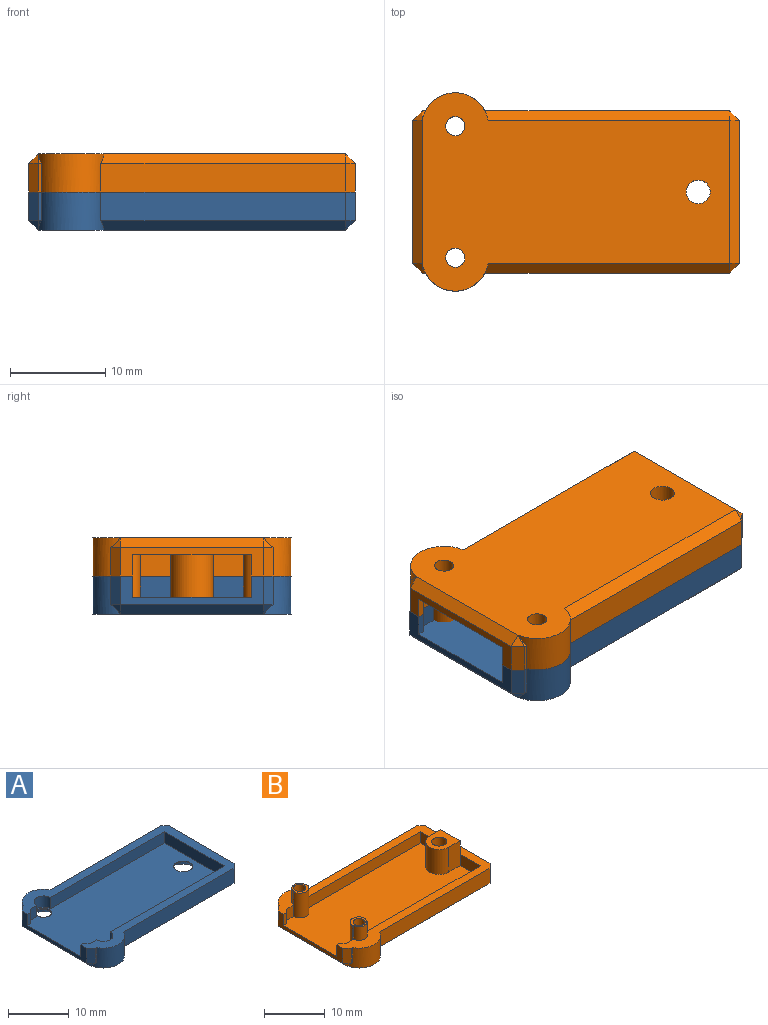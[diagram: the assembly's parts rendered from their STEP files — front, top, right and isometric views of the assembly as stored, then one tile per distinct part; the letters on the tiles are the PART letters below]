
ASSEMBLY  parts=2 mates=3
PART A: 42 faces, bbox 34.3x20.8x4 mm
  f0: plane 15x3mm, normal (-1,0,0), area 17.1mm2, adj f4,f13,f21,f22,f32,f35,f36
  f1: cylinder r=1.3mm len=2.6mm, axis (0,0,-1), area 2mm2, adj f22,f39
  f2: cylinder r=1.55mm len=3.1mm, axis (0,0,-1), area 1.5mm2, adj f22,f41
  f3: cylinder r=1.3mm len=2.6mm, axis (0,0,-1), area 2mm2, adj f22,f40
  f4: plane 34.25x20.8mm, normal (0,0,1), area 141.4mm2, adj f0,f5,f6,f7,f8,f9,f10,f11
  f5: plane 3x0.34mm, normal (0,-1,0), area 1mm2, adj f4,f6,f32,f33
  f6: cylinder r=3.5mm len=6.9mm, axis (0,0,-1), area 31.8mm2, adj f4,f5,f7,f12,f25,f33
  f7: plane 25.69x3mm, normal (0,-1,0), area 77.1mm2, adj f4,f6,f25,f26
  f8: plane 15x3mm, normal (1,0,0), area 45mm2, adj f4,f26,f28,f29
  f9: plane 25.69x3mm, normal (0,1,0), area 77.1mm2, adj f4,f10,f29,f31
  f10: cylinder r=3.5mm len=6.9mm, axis (0,0,-1), area 31.8mm2, adj f4,f9,f11,f12,f31,f38
  f11: plane 3x0.34mm, normal (0,1,0), area 1mm2, adj f4,f10,f35,f38
  f12: plane 32.25x20.8mm, normal (0,0,-1), area 433.4mm2, adj f6,f10,f25,f28,f31,f33,f36,f38
  f13: plane 2.25x0.7mm, normal (0,1,0), area 1.6mm2, adj f0,f4,f22,f23
  f14: plane 2.25x1.45mm, normal (0,1,0), area 3.3mm2, adj f4,f15,f22,f23
  f15: cylinder r=1.6mm len=3.2mm, axis (0,0,1), area 11.3mm2, adj f4,f14,f16,f22
  f16: plane 26.5x2.25mm, normal (0,1,0), area 59.6mm2, adj f4,f15,f17,f22
  f17: plane 13.8x2.25mm, normal (-1,0,0), area 31mm2, adj f4,f16,f18,f22
  f18: plane 26.5x2.25mm, normal (0,-1,0), area 59.6mm2, adj f4,f17,f19,f22
  f19: cylinder r=1.6mm len=3.2mm, axis (0,0,1), area 11.3mm2, adj f4,f18,f20,f22
  f20: plane 2.25x1.45mm, normal (0,-1,0), area 3.3mm2, adj f4,f19,f22,f24
  f21: plane 2.25x0.7mm, normal (0,-1,0), area 1.6mm2, adj f0,f4,f22,f24
  f22: plane 32.55x17mm, normal (0,0,1), area 437.6mm2, adj f0,f1,f2,f3,f13,f14,f15,f16
  f23: plane 2.25x0.7mm, normal (0.71,0.71,0), area 2.2mm2, adj f4,f13,f14,f22
  f24: plane 2.25x0.7mm, normal (0.71,-0.71,0), area 2.2mm2, adj f4,f20,f21,f22
  f25: plane 25.69x1mm, normal (0,-0.71,-0.71), area 36.1mm2, adj f6,f7,f12,f27
  f26: plane 3x1mm, normal (0.71,-0.71,0), area 4.2mm2, adj f4,f7,f8,f27
  f27: plane 1x1mm, normal (0.58,-0.58,-0.58), area 0.9mm2, adj f25,f26,f28
  f28: plane 15x1mm, normal (0.71,0,-0.71), area 21.2mm2, adj f8,f12,f27,f30
  f29: plane 3x1mm, normal (0.71,0.71,0), area 4.2mm2, adj f4,f8,f9,f30
  f30: plane 1x1mm, normal (0.58,0.58,-0.58), area 0.9mm2, adj f28,f29,f31
  f31: plane 25.69x1mm, normal (0,0.71,-0.71), area 36.1mm2, adj f9,f10,f12,f30
  f32: plane 3x1mm, normal (-0.71,-0.71,0), area 4.2mm2, adj f0,f4,f5,f34
  f33: plane 1x1mm, normal (0,-0.71,-0.71), area 0.2mm2, adj f5,f6,f12,f34
  f34: plane 1x1mm, normal (-0.58,-0.58,-0.58), area 0.9mm2, adj f32,f33,f36
  f35: plane 3x1mm, normal (-0.71,0.71,0), area 4.2mm2, adj f0,f4,f11,f37
  f36: plane 15x1mm, normal (-0.71,0,-0.71), area 21.2mm2, adj f0,f12,f34,f37
  f37: plane 1x1mm, normal (-0.58,0.58,-0.58), area 0.9mm2, adj f35,f36,f38
  f38: plane 1x1mm, normal (0,0.71,-0.71), area 0.2mm2, adj f10,f11,f12,f37
  f39: cone r=2.8mm half-angle=45deg, axis (0,0,-1), area 27.3mm2, adj f1,f12
  f40: cone r=1.3mm half-angle=45deg, axis (0,0,-1), area 27.3mm2, adj f3,f12
  f41: cone r=3.15mm half-angle=45deg, axis (0,0,-1), area 33.4mm2, adj f2,f12
PART B: 53 faces, bbox 34.3x20.8x6.8 mm
  f0: plane 26.6x2.25mm, normal (0,1,0), area 59.9mm2, adj f1,f8,f19,f49
  f1: plane 32.55x13.8mm, normal (0,0,1), area 421mm2, adj f0,f2,f3,f4,f17,f18,f19,f20
  f2: plane 26.6x2.25mm, normal (0,-1,0), area 59.9mm2, adj f1,f3,f8,f45
  f3: plane 4.65x2.25mm, normal (-1,0,0), area 10.5mm2, adj f1,f2,f8,f39
  f4: plane 15x3mm, normal (-1,0,0), area 17.1mm2, adj f1,f8,f17,f21,f31,f34,f35
  f5: cylinder r=1mm len=6.75mm, axis (0,0,-1), area 42.4mm2, adj f16,f47
  f6: cylinder r=1.25mm len=6.75mm, axis (0,0,-1), area 53mm2, adj f16,f42
  f7: cylinder r=1mm len=6.75mm, axis (0,0,-1), area 42.4mm2, adj f16,f52
  f8: plane 34.25x20.8mm, normal (0,0,1), area 144.1mm2, adj f0,f2,f3,f4,f9,f10,f11,f12
  f9: plane 3x0.34mm, normal (0,-1,0), area 1mm2, adj f8,f10,f31,f32
  f10: cylinder r=3.5mm len=6.9mm, axis (0,0,-1), area 31.8mm2, adj f8,f9,f11,f16,f24,f32
  f11: plane 25.69x3mm, normal (0,-1,0), area 77.1mm2, adj f8,f10,f24,f25
  f12: plane 15x3mm, normal (1,0,0), area 45mm2, adj f8,f25,f27,f28
  f13: plane 25.69x3mm, normal (0,1,0), area 77.1mm2, adj f8,f14,f28,f30
  f14: cylinder r=3.5mm len=6.9mm, axis (0,0,-1), area 31.8mm2, adj f8,f13,f15,f16,f30,f37
  f15: plane 3x0.34mm, normal (0,1,0), area 1mm2, adj f8,f14,f34,f37
  f16: plane 32.25x20.8mm, normal (0,0,-1), area 502.7mm2, adj f5,f6,f7,f10,f14,f24,f27,f30
  f17: plane 2.25x0.7mm, normal (0,1,0), area 1.6mm2, adj f1,f4,f8,f22
  f18: plane 2.25x1.55mm, normal (0,1,0), area 3.5mm2, adj f1,f8,f22,f49
  f19: plane 4.65x2.25mm, normal (-1,0,0), area 10.5mm2, adj f0,f1,f8,f41
  f20: plane 2.25x1.55mm, normal (0,-1,0), area 3.5mm2, adj f1,f8,f23,f45
  f21: plane 2.25x0.7mm, normal (0,-1,0), area 1.6mm2, adj f1,f4,f8,f23
  f22: plane 2.25x0.7mm, normal (0.71,0.71,0), area 2.2mm2, adj f1,f8,f17,f18
  f23: plane 2.25x0.7mm, normal (0.71,-0.71,0), area 2.2mm2, adj f1,f8,f20,f21
  f24: plane 25.69x1mm, normal (0,-0.71,-0.71), area 36.1mm2, adj f10,f11,f16,f26
  f25: plane 3x1mm, normal (0.71,-0.71,0), area 4.2mm2, adj f8,f11,f12,f26
  f26: plane 1x1mm, normal (0.58,-0.58,-0.58), area 0.9mm2, adj f24,f25,f27
  f27: plane 15x1mm, normal (0.71,0,-0.71), area 21.2mm2, adj f12,f16,f26,f29
  f28: plane 3x1mm, normal (0.71,0.71,0), area 4.2mm2, adj f8,f12,f13,f29
  f29: plane 1x1mm, normal (0.58,0.58,-0.58), area 0.9mm2, adj f27,f28,f30
  f30: plane 25.69x1mm, normal (0,0.71,-0.71), area 36.1mm2, adj f13,f14,f16,f29
  f31: plane 3x1mm, normal (-0.71,-0.71,0), area 4.2mm2, adj f4,f8,f9,f33
  f32: plane 1x1mm, normal (0,-0.71,-0.71), area 0.2mm2, adj f9,f10,f16,f33
  f33: plane 1x1mm, normal (-0.58,-0.58,-0.58), area 0.9mm2, adj f31,f32,f35
  f34: plane 3x1mm, normal (-0.71,0.71,0), area 4.2mm2, adj f4,f8,f15,f36
  f35: plane 15x1mm, normal (-0.71,0,-0.71), area 21.2mm2, adj f4,f16,f33,f36
  f36: plane 1x1mm, normal (-0.58,0.58,-0.58), area 0.9mm2, adj f34,f35,f37
  f37: plane 1x1mm, normal (0,0.71,-0.71), area 0.2mm2, adj f14,f15,f16,f36
  f38: plane 4.5x2.75mm, normal (1,0,0), area 12.4mm2, adj f8,f39,f41,f42
  f39: plane 5x2.6mm, normal (0,1,0), area 13mm2, adj f1,f3,f38,f40,f42
  f40: cylinder r=2.25mm len=5mm, axis (0,0,-1), area 35.3mm2, adj f1,f39,f41,f42
  f41: plane 5x2.6mm, normal (0,-1,0), area 13mm2, adj f1,f19,f38,f40,f42
  f42: plane 4.85x4.5mm, normal (0,0,1), area 14.7mm2, adj f6,f38,f39,f40,f41
  f43: cylinder r=1.3mm len=2.75mm, axis (0,0,-1), area 11.2mm2, adj f8,f44,f46,f47
  f44: plane 2.75x0.2mm, normal (0,1,0), area 0.6mm2, adj f8,f43,f45,f47
  f45: cylinder r=1.5mm len=5mm, axis (0,0,-1), area 23.6mm2, adj f1,f2,f20,f44,f46,f47
  f46: plane 2.75x0.2mm, normal (0,1,0), area 0.6mm2, adj f8,f43,f45,f47
  f47: plane 3x2.8mm, normal (0,0,1), area 3mm2, adj f5,f43,f44,f45,f46
  f48: cylinder r=1.3mm len=2.75mm, axis (0,0,-1), area 11.2mm2, adj f8,f50,f51,f52
  f49: cylinder r=1.5mm len=5mm, axis (0,0,-1), area 23.6mm2, adj f0,f1,f18,f50,f51,f52
  f50: plane 2.75x0.2mm, normal (0,-1,0), area 0.6mm2, adj f8,f48,f49,f52
  f51: plane 2.75x0.2mm, normal (0,-1,0), area 0.6mm2, adj f8,f48,f49,f52
  f52: plane 3x2.8mm, normal (0,0,1), area 3mm2, adj f7,f48,f49,f50,f51
PLACE A rot(axis=(1,0,0),0deg) t=(1.2,-65.44,18.69)mm
PLACE B rot(axis=(-1,0,0),180deg) t=(1.2,-48.44,26.69)mm
MATE planar B.f7 <-> A.f3  axis (0,0,-1) through (5.65,-50.04,22.69)mm
MATE planar A.f8 <-> B.f12  axis (1,0,0) through (35.45,-56.94,22.69)mm
MATE planar B.f11 <-> A.f9  axis (0,1,0) through (21.61,-48.44,24.19)mm
